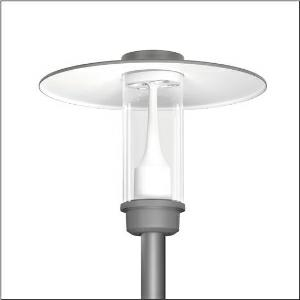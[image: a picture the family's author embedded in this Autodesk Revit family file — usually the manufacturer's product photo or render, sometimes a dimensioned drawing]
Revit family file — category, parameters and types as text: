
# Revit family: litepole_2_iq___p1_0a_5xa5425lf14hp_dc73
name_source: partatom
category: Lighting Fixtures
units: mm (PartAtom-declared; Revit-internal decimal feet)

## family parameters
Cut with Voids When Loaded = No
Host = Face
Light Source = No
Part Type = Normal
Room Calculation Point = No
Round Connector Dimension = Use Diameter
Shared = No

## types (1)
- --- (1 x LED, 4940 lm, 33.6 W, 4000K)
    Apparent Load = 34 VA
    CIE Flux Codes = 32 62 90 96 100
    Color Rendering = 70
    Color Temperature = 4000K
    Default Elevation = 1800 mm
    Description = Litepole 2 iQ, mast luminaire, Module 540 iQ-SR, primary light control with 3 zone facetted reflector, of plastic, silver coated, highly specular, structured, primary optical cover: cover, of PMMA, transparent, light distribution: P1.0a, light emission: direct distribution, primary light characteristic: strongly asymmetric, installation type: post-top, LED, High Power LED, rated luminous flux: 4.940lm, luminous efficacy: 147lm/W, light colour: 740, colour temperature: 4000K, control gear: iQ Street-Remote, control: pre-setting: logarithmic dimming characteristic, Street-Remote, Auto-Match, Temp-Guard, Lumen-Switch, Night-Set, Smart-Wire, Light-Fading, Desk-Remote (wireless, voltage-free reading and setting of iQ features in the workshop via application-optimized NFC function/RFID function), optimised constant luminous flux control (CLO 2.0), with terminal, 6-pole, max. 2.5mm², mains connection: 230..240V, AC, 50/60Hz, start of lifetime: 34W, end of service life: 36W, reduction: 15W, luminaire housing, upper part, of aluminium, coated, Siteco® metallic grey (DB 702S), diameter: 750mm, height: 590mm, spigot size: d x l = 76 x 70mm (post-top) | with reducer (optional accessory) 60 x 70mm, mounting height: 3..5m, post-top mast mounting element, of diecast aluminium, coated, Siteco® metallic grey (DB 702S), Module 540 iQ-SR, traffic white (RAL 9016), equipment: Power, protection rating (complete): IP65, insulation class (complete): insulation class II (safety insulation), certification: CE, ENEC, VDE, packaging unit: 1 piece

Light Distribution: P1.0a
    Height = 590 mm
    Lamp = 1 x LED
    Lamp Light Flux = 4940 lm
    Lamp Power = 33.6 W
    Lamp count = 1
    Length = 750 mm
    Luminous efficacy = 147 lm/W
    Manufacturer = Siteco
    ModVariant = No
    Model = 5XA5425LF14HP
    Number of Poles = 1
    OnlyDefault = Yes
    Power Factor = 1
    Product Name = Litepole 2 iQ | P1.0a
    Product group = mast luminaire | pylon top
    ProductGroupID = 6100
    Protection Class = Protection class II
    Protection Degree = IP 65
    RLX_Detail_Level = 1
    RLX_Emergency_Light_Flux = 0 lm
    RLX_Emergency_Type = 0
    RLX_Emergency_Type_DB = No
    RlxData = <blob elided: 32005 chars, md5=1ab7c1e6>
    Socket = socket
    Standby Power = 0 W
    System Light Flux = 4940 lm
    System Power = 34 W
    Type Comments = factory setting: luminous flux: 100 % | dim-lin: 254 | 695 mA
    Type Image = l_1006518.jpg
    URL = http://relux.com
    VarID = @adj_192334
    Voltage = 0 V
    Weight = 0.00 kg
    Width = 0 mm  [stored 0 ft]

note: [stored X ft] marks values corroborated as IEEE doubles in the binary element streams (Revit-internal decimal feet)

## geometry (parser evidence)
native form markers: Blend x4, Sweep x10
no freeform markers — native parametric forms only
